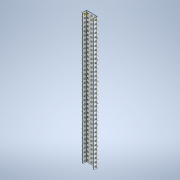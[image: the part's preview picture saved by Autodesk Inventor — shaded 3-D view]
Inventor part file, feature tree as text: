
AUTODESK INVENTOR PART (.ipt)
format: ipt  version: 2020 (Build 240168000, 168)  size: 1,440,256 bytes
history: native  units: in
note: dims shown in document units (in); Inventor stores cm internally (conversion verified against a paired STEP export)
features: other x178, plane x4, pattern_linear x3, sheet_metal_op x1
ambient origin geometry x8: Origin, YZ Plane, XZ Plane, XY Plane, X Axis, Y Axis, Z Axis, Center Point
bodies: Solid1 (feature_tree)
feature tree (186):
  plane  "Work Plane2"
  plane  "Work Plane1"
  other  "Work Point1"
  other  "Work Point2"
  other  "Work Axis1"
  other  "Work Axis2"
  other  "Work Axis3"
  pattern_linear  "Rectangular Pattern1"  Count1=35 Spacing1=0.5in
  pattern_linear  "Rectangular Pattern2"  Count1=35 Spacing1=0.5in
  pattern_linear  "Rectangular Pattern3"  Count1=35 Spacing1=0.5in
  plane  "Work Plane3"
  plane  "Work Plane4"
  other  "Work Point3"
  other  "Work Axis4"
  other  "Work Axis5"
  other  "Work Axis6"
  other  "Work Axis7"
  other  "Work Axis8"
  other  "Work Axis9"
  other  "Work Axis10"
  other  "Work Axis11"
  other  "Work Axis12"
  other  "Work Axis13"
  other  "Work Axis14"
  other  "Work Axis15"
  other  "Work Axis16"
  other  "Work Axis17"
  other  "Work Axis18"
  other  "Work Axis19"
  other  "Work Axis20"
  other  "Work Axis21"
  other  "Work Axis22"
  other  "Work Axis23"
  other  "Work Axis24"
  other  "Work Axis25"
  other  "Work Axis26"
  other  "Work Axis27"
  other  "Work Axis28"
  other  "Work Axis29"
  other  "Work Axis30"
  other  "Work Axis31"
  other  "Work Axis32"
  other  "Work Axis33"
  other  "Work Axis34"
  other  "Work Axis35"
  other  "Work Axis36"
  other  "Work Axis37"
  other  "Work Axis38"
  other  "Work Axis39"
  other  "Work Axis40"
  other  "Work Axis41"
  other  "Work Axis42"
  other  "Work Axis43"
  other  "Work Axis44"
  other  "Work Axis45"
  other  "Work Axis46"
  other  "Work Axis47"
  other  "Work Axis48"
  other  "Work Axis49"
  other  "Work Axis50"
  other  "Work Axis51"
  other  "Work Axis52"
  other  "Work Axis53"
  other  "Work Axis54"
  other  "Work Axis55"
  other  "Work Axis56"
  other  "Work Axis57"
  other  "Work Axis58"
  other  "Work Axis59"
  other  "Work Axis60"
  other  "Work Axis61"
  other  "Work Axis62"
  other  "Work Axis63"
  other  "Work Axis64"
  other  "Work Axis65"
  other  "Work Axis66"
  other  "Work Axis67"
  other  "Work Axis68"
  other  "Work Axis69"
  other  "Work Axis70"
  other  "Work Axis71"
  other  "Work Axis72"
  other  "Work Axis73"
  other  "Work Axis74"
  other  "Work Axis75"
  other  "Work Axis76"
  other  "Work Axis77"
  other  "Work Axis78"
  other  "Work Axis79"
  other  "Work Axis80"
  other  "Work Axis81"
  other  "Work Axis82"
  other  "Work Axis83"
  other  "Work Axis84"
  other  "Work Axis85"
  other  "Work Axis86"
  other  "Work Axis87"
  other  "Work Axis88"
  other  "Work Axis89"
  other  "Work Axis90"
  other  "Work Axis91"
  other  "Work Axis92"
  other  "Work Axis93"
  other  "Work Axis94"
  other  "Work Axis95"
  other  "Work Axis96"
  other  "Work Axis97"
  other  "Work Axis98"
  other  "Work Axis99"
  other  "Work Axis100"
  other  "Work Axis101"
  other  "Work Axis102"
  other  "Work Axis103"
  other  "Work Axis104"
  other  "Work Axis105"
  other  "Work Axis106"
  other  "Work Axis107"
  other  "Work Axis108"
  other  "Work Axis109"
  other  "Work Axis110"
  other  "Work Axis111"
  other  "Work Axis112"
  other  "Work Axis113"
  other  "Work Axis114"
  other  "Work Axis115"
  other  "Work Axis116"
  other  "Work Axis117"
  other  "Work Axis118"
  other  "Work Axis119"
  other  "Work Axis120"
  other  "Work Axis121"
  other  "Work Axis122"
  other  "Work Axis123"
  other  "Work Axis124"
  other  "Work Axis125"
  other  "Work Axis126"
  other  "Work Axis127"
  other  "Work Axis128"
  other  "Work Axis129"
  other  "Work Axis130"
  other  "Work Axis131"
  other  "Work Axis132"
  other  "Work Axis133"
  other  "Work Axis134"
  other  "Work Axis135"
  other  "Work Axis136"
  other  "Work Axis137"
  other  "Work Axis138"
  other  "Work Axis139"
  other  "Work Axis140"
  other  "Work Axis141"
  other  "Work Axis142"
  other  "Work Axis143"
  other  "Work Axis144"
  other  "Work Axis145"
  other  "Work Axis146"
  other  "Work Axis147"
  other  "Work Axis148"
  other  "Work Axis149"
  other  "Work Axis150"
  other  "Work Axis151"
  other  "Work Axis152"
  other  "Work Axis153"
  other  "Work Axis154"
  other  "Work Axis155"
  other  "Work Axis156"
  other  "Work Axis157"
  other  "Work Axis158"
  other  "Work Axis159"
  other  "Work Axis160"
  other  "Work Axis161"
  other  "Work Axis162"
  other  "Work Axis163"
  other  "Work Axis164"
  other  "Work Axis165"
  other  "Work Axis166"
  other  "Work Axis167"
  other  "Work Axis168"
  other  "Work Axis169"
  other  "Work Axis170"
  other  "Work Axis171"
  other  "Work Axis172"
  other  "Work Axis173"
  other  "Work Axis174"
  other  "Work Axis175"
  sheet_metal_op  "Fold1"
